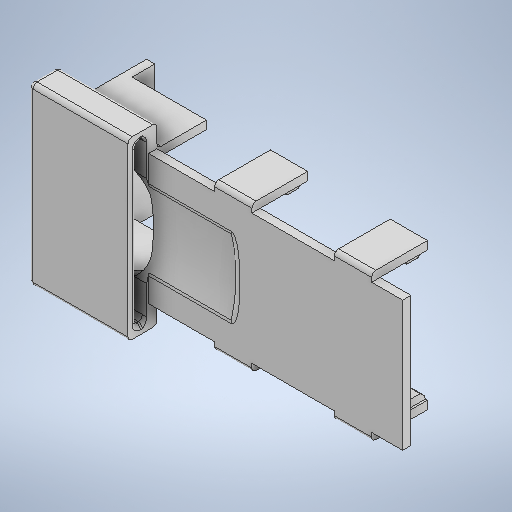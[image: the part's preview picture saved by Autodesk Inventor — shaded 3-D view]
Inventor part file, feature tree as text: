
AUTODESK INVENTOR PART (.ipt)
format: ipt  version: 2025 (Build 290162000, 162)  size: 524,800 bytes
history: native  units: in
note: dims shown in document units (in); Inventor stores cm internally (conversion verified against a paired STEP export)
features: reference x27, extrude x12, sketch x5, fillet x4, other x3, plane x2, chamfer x1
ambient origin geometry x8: Origin, YZ Plane, XZ Plane, XY Plane, X Axis, Y Axis, Z Axis, Center Point
bodies: Solid1 (feature_tree)
feature tree (54):
  extrude  "Extrusion1"  Depth=0.0157in TaperAngle=0.0deg
  sketch  "Sketch2"  dims[d0=0.0394in d1=0.0157in d2=0.0in]
  plane  "Work Plane1"
  extrude  "Extrusion2"  Depth=4.0in TaperAngle=0.0deg
  extrude  "Extrusion3"  Depth=0.0157in TaperAngle=0.0deg
  extrude  "Extrusion4"  Depth=0.0079in
  plane  "Work Plane2"
  extrude  "Extrusion5"  Depth=0.0157in
  extrude  "Extrusion6"  TaperAngle=0.0deg  [1 undecoded]
  extrude  "Extrusion7"  Depth=0.0157in
  extrude  "Extrusion8"  Depth=0.0157in
  extrude  "Extrusion9"  Depth=0.0157in
  extrude  "Extrusion10"  TaperAngle=0.0deg  [1 undecoded]
  extrude  "Extrusion11"  Depth=0.0157in
  fillet  "Fillet9"  Radius=0.0039in
  fillet  "Fillet10"  Radius=0.0118in
  extrude  "Extrusion12"  Depth=0.0118in
  fillet  "Fillet12"  Radius=0.3346in
  fillet  "Fillet13"  Radius=0.0315in
  chamfer  "Chamfer3"  Distance=0.1673in
  reference  "Reference1"
  reference  "Reference2"
  reference  "Reference3"
  reference  "Reference4"
  reference  "Reference5"
  sketch  "Sketch3"  dims[d3=0.0315in d4=4.0in d5=0.0in]
  reference  "Reference6"
  reference  "Reference7"
  reference  "Reference8"
  reference  "Reference9"
  reference  "Reference10"
  reference  "Reference11"
  reference  "Reference12"
  reference  "Reference13"
  sketch  "Sketch4"  dims[d6=0.0157in d7=0.0in d8=0.0157in d9=0.0in]
  reference  "Reference14"
  reference  "Reference15"
  reference  "Reference16"
  reference  "Reference17"
  reference  "Reference18"
  reference  "Reference19"
  reference  "Reference20"
  reference  "Reference21"
  reference  "Reference22"
  reference  "Reference23"
  reference  "Reference24"
  reference  "Reference25"
  reference  "Reference26"
  reference  "Reference27"
  sketch  "Sketch10"  dims[d10=0.126in d11=0.0in d12=0.0079in]
  sketch  "Sketch13"  dims[d13=0.0157in d14=0.0in d15=0.0039in d16=0.0in d17=0.0039in d18=0.0039in d19=0.0039in d20=0.0in d21=0.0039in d22=0.0039in d23=0.0118in d24=-0.0687in d25=0.0118in d26=-0.0687in d27=0.3346in d29=0.0315in d30=0.1673in d31=0.0394in d32=0.0in d34=0.0157in d36=0.0157in d37=0.0197in d38=0.1457in d39=0.0in d46=0.1457in d47=0.0in d65=0.0157in d66=0.0in d67=0.0157in d70=0.0591in d71=0.0079in d73=0.0in d74=0.1378in d75=0.563in d76=0.315in d77=0.0in d79=0.0197in d81=0.0079in d82=0.0079in d83=0.0197in d84=0.0059in d85=0.0787in d86=45.0deg d68=0.0344in d69=0.0197in]
  parser-record x1  (decoder bookkeeping rows leaked as tree rows — omitted from the tree; the rows remain in map.json)
  other  "np2_full_assembly.iam"
  other  "np2_main_chassis:1"
note: 2 required parameter values undecoded (feature->parameter linkage not recoverable at this tier; creation-order binding heuristic only, values carry confidence <= 0.55)
note: 1 file-system path scrubbed to <path> (originals preserved in map.json)
